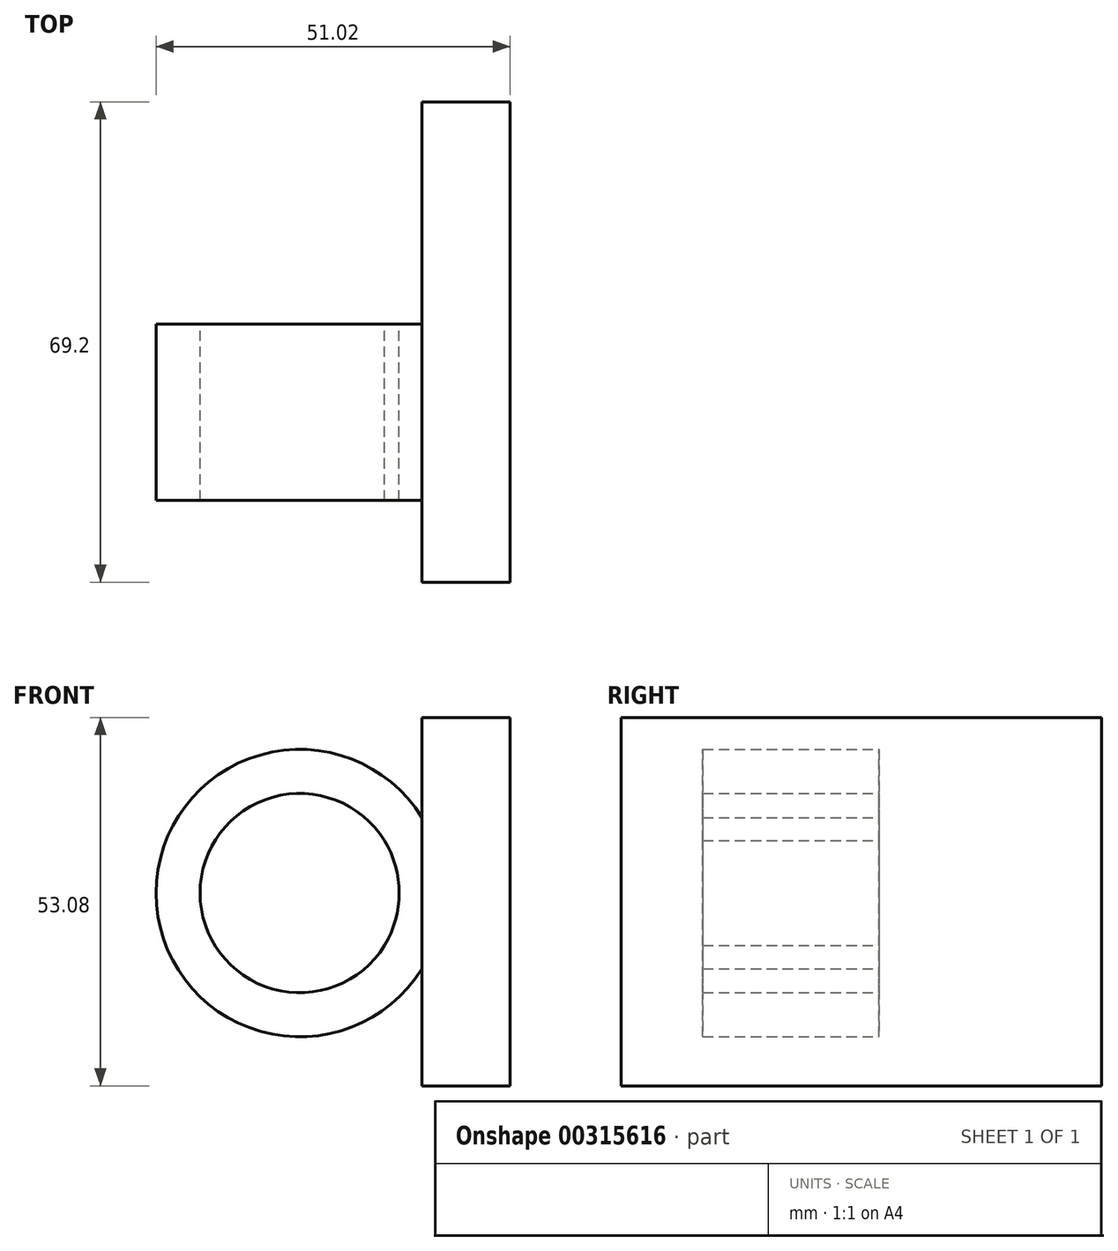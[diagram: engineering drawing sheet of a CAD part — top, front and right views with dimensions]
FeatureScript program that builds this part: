
annotation { "Feature Type Name" : "Feature", "Feature Type Description" : "" }
export const myFeature = defineFeature(function(context is Context, id is Id, definition is map)
    precondition{}
    {
        {
            var Q0;
            Q0=qCreatedBy(makeId("Right.planeOp"),FACE);
            var sketch = newSketch(context, id + "F0", { "sketchPlane" : qUnion([Q0])});
            skLineSegment(sketch, "E0.bottom", {"start": v(-37.16, 26.16) * mm, "end": v(32.04, 26.16) * mm});
            skLineSegment(sketch, "E0.top", {"start": v(-37.16, -26.92) * mm, "end": v(32.04, -26.92) * mm});
            skLineSegment(sketch, "E0.left", {"start": v(-37.16, 26.16) * mm, "end": v(-37.16, -26.92) * mm});
            skLineSegment(sketch, "E0.right", {"start": v(32.04, 26.16) * mm, "end": v(32.04, -26.92) * mm});
            skSolve(sketch);
        }
        {
            var Q0;
            Q0 = qSketchRegion(id + "F0", true);
            extrude(context, id + "F1", {"entities" : qUnion([Q0]), "depth" : 12.7 * mm});
        }
        {
            var Q0;
            Q0=qCreatedBy(makeId("Front.planeOp"),FACE);
            var sketch = newSketch(context, id + "F2", { "sketchPlane" : qUnion([Q0])});
            skArc(sketch, "E1", {"start": v(0, 11.76) * mm, "mid": v(-38.32, 0.85) * mm, "end": v(0, -10.05) * mm});
            skLineSegment(sketch, "E2", {"start": v(0, 11.76) * mm, "end": v(0, -10.05) * mm});
            skSolve(sketch);
        }
        {
            var Q0;
            Q0 = qSketchRegion(id + "F2", true);
            extrude(context, id + "F3", {"entities" : qUnion([Q0]), "depth" : 25.4 * mm});
        }
        {
            var Q0;
            Q0=qCreatedBy(makeId("Front.planeOp"),FACE);
            var sketch = newSketch(context, id + "F4", { "sketchPlane" : qUnion([Q0])});
            skArc(sketch, "E3.0", {"start": v(-5.4, 8.41) * mm, "mid": v(-31.97, 0.85) * mm, "end": v(-5.4, -6.7) * mm});
            skArc(sketch, "E4", {"start": v(-5.4, -6.7) * mm, "mid": v(-3.3, 0.85) * mm, "end": v(-5.4, 8.41) * mm});
            skSolve(sketch);
        }
        {
            var Q0;
            Q0=qCreatedBy(makeId("Front.planeOp"),FACE);
            var sketch = newSketch(context, id + "F5", { "sketchPlane" : qUnion([Q0])});
            skLineSegment(sketch, "E5", {"start": v(0, 12.13) * mm, "end": v(0, -9.67) * mm});
            skSolve(sketch);
        }
        {
            var Q0;
            Q0=sQuery(id+"F5.wireOp",EDGE,"E5");
            extrude(context, id + "F6", {"bodyType" : ToolBodyType.SURFACE, "surfaceEntities" : qUnion([Q0]), "depth" : 25.4 * mm});
        }
        {
            var Q0;
            Q0 = qSketchRegion(id + "F2", true);
            extrude(context, id + "F7", {"entities" : qUnion([Q0]), "depth" : 25.4 * mm});
        }
        {
            var Q0;
            Q0 = qSketchRegion(id + "F4", true);
            extrude(context, id + "F8", {"entities" : qUnion([Q0]), "operationType" : NewBodyOperationType.REMOVE, "endBound" : BoundingType.THROUGH_ALL, "depth" : 25.4 * mm});
        }
        {
            var Q0;
            Q0 = qSketchRegion(id + "F0", true);
            extrude(context, id + "F9", {"entities" : qUnion([Q0]), "depth" : 12.7 * mm});
        }
    });
